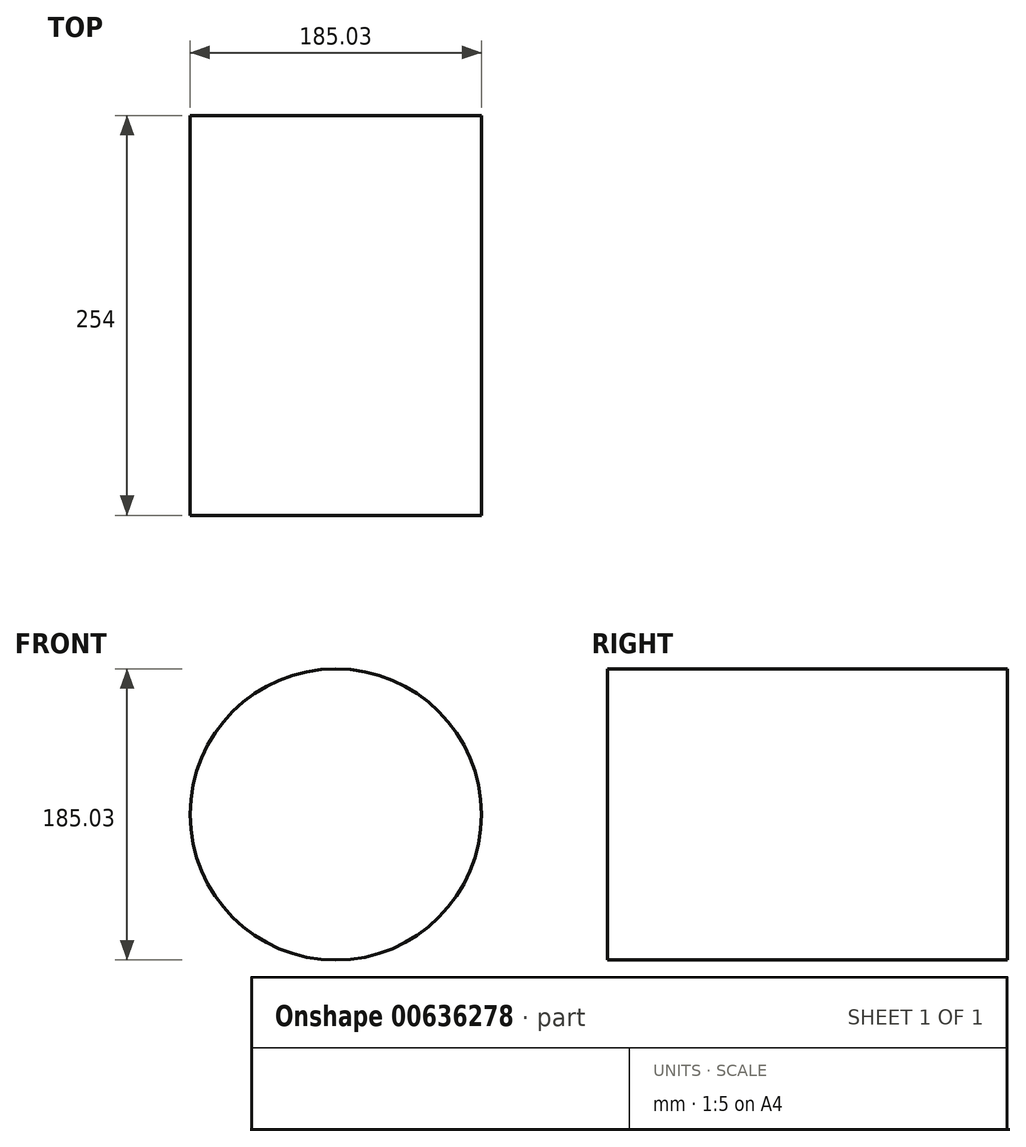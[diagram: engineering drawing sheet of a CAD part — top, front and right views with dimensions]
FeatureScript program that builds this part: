
annotation { "Feature Type Name" : "Feature", "Feature Type Description" : "" }
export const myFeature = defineFeature(function(context is Context, id is Id, definition is map)
    precondition{}
    {
        {
            var Q0;
            Q0=qCreatedBy(makeId("Front.planeOp"),FACE);
            var sketch = newSketch(context, id + "F0", { "sketchPlane" : qUnion([Q0])});
            skCircle(sketch, "E0", {"center": v(-46.54, 79.96) * mm, "radius": 92.51 * mm});
            skPoint(sketch, "E0.first.point", {"position": v(0, 0) * mm});
            skPoint(sketch, "E0.second.point", {"position": v(44.3, 97.46) * mm});
            skPoint(sketch, "E0.third.point", {"position": v(40.64, 48.99) * mm});
            skSolve(sketch);
        }
        {
            var Q0;
            Q0 = qSketchRegion(id + "F0", true);
            extrude(context, id + "F1", {"entities" : qUnion([Q0]), "depth" : 254 * mm, "offsetDistance" : 25.4 * mm});
        }
        {
            var Q0;
            Q0=makeQuery(id+"F1.opExtrude","CAP_FACE",FACE,{"disambiguationData":[OSD([sQuery(id+"F0.wireOp",EDGE,"E0")])],"isStart":true});
            var sketch = newSketch(context, id + "F2", { "sketchPlane" : qUnion([Q0])});
            skCircle(sketch, "E1", {"center": v(46.54, 79.96) * mm, "radius": 16.56 * mm});
            skSolve(sketch);
        }
        {
            var Q0;
            Q0 = qSketchRegion(id + "F2", true);
            extrude(context, id + "F3", {"entities" : qUnion([Q0]), "operationType" : NewBodyOperationType.ADD, "oppositeDirection" : true, "depth" : 254 * mm, "offsetDistance" : 25.4 * mm});
        }
    });
